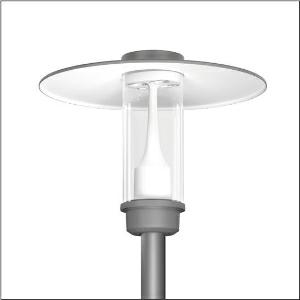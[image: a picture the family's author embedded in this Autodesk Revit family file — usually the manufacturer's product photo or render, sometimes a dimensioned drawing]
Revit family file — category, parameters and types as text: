
# Revit family: litepole_2_iq___p1_0a_5xa5425nf14h_2791
name_source: partatom
category: Lighting Fixtures
units: mm (PartAtom-declared; Revit-internal decimal feet)

## family parameters
Cut with Voids When Loaded = No
Host = Face
Light Source = No
Part Type = Normal
Room Calculation Point = No
Round Connector Dimension = Use Diameter
Shared = No

## types (1)
- --- (1 x LED, 1520 lm, 11.8 W, 2700K)
    Apparent Load = 12 VA
    CIE Flux Codes = 33 62 89 96 100
    Color Rendering = 70
    Color Temperature = 2700K
    Default Elevation = 1800 mm
    Description = Litepole 2 iQ, mast luminaire, Module 540 iQ-SR, primary light control with 3 zone facetted reflector, of plastic, silver coated, highly specular, structured, primary optical cover: cover, of PMMA, transparent, light distribution: P1.0a, light emission: direct distribution, primary light characteristic: strongly asymmetric, installation type: post-top, LED, High Power LED, rated luminous flux: 1.520lm, luminous efficacy: 129lm/W, light colour: 727, colour temperature: 2700K, control gear: ECG iQ, control: presetting dimming logarithmic, Street-Remote, Auto-Match, Temp-Guard, Lumen-Switch, Night-Set, Smart-Wire, Light-Fading, Desk-Remote (wireless, voltage-free reading and setting of iQ features in the workshop via application-optimized NFC function/RFID function), optimised constant luminous flux control (CLO 2.0), with terminal, 6-pole, max. 2.5mm², mains connection: 230..240V, AC, 50/60Hz, start of lifetime: 12W, end of service life: 12W, reduction: 6W, luminaire housing, upper part, of aluminium, coated, Siteco® metallic grey (DB 702S), diameter: 750mm, height: 590mm, spigot size: d x l = 76 x 70mm (post-top) | with reducer (optional accessory) 60 x 70mm, post-top mast mounting element, of diecast aluminium, coated, Siteco® metallic grey (DB 702S), Module 540 iQ-SR, traffic white (RAL 9016), equipment: standard, protection rating (complete): IP65, insulation class (complete): insulation class II (safety insulation), certification: CE, ENEC, VDE, packaging unit: 1 piece

Light Distribution: P1.0a
    Height = 590 mm
    Lamp = 1 x LED
    Lamp Light Flux = 1520 lm
    Lamp Power = 11.8 W
    Lamp count = 1
    Length = 750 mm
    Luminous efficacy = 129 lm/W
    Manufacturer = Siteco
    ModVariant = No
    Model = 5XA5425NF14H
    Number of Poles = 1
    OnlyDefault = Yes
    Power Factor = 1
    Product Name = Litepole 2 iQ | P1.0a
    Product group = mast luminaire | pylon top
    ProductGroupID = 6100
    Protection Class = Protection class II
    Protection Degree = IP 65
    RLX_Detail_Level = 1
    RLX_Emergency_Light_Flux = 0 lm
    RLX_Emergency_Type = 0
    RLX_Emergency_Type_DB = No
    RlxData = <blob elided: 138057 chars, md5=5de45a06>
    Socket = socket
    Standby Power = 0 W
    System Light Flux = 1520 lm
    System Power = 12 W
    Type Comments = factory setting: luminous flux: 100 % | dim-lin: 254 | 472 mA
    Type Image = l_1006518.jpg
    URL = http://relux.com
    VarID = @adj_102557
    Voltage = 0 V
    Weight = 0.00 kg
    Width = 0 mm  [stored 0 ft]

note: [stored X ft] marks values corroborated as IEEE doubles in the binary element streams (Revit-internal decimal feet)

## geometry (parser evidence)
native form markers: Blend x4, Sweep x10
no freeform markers — native parametric forms only
